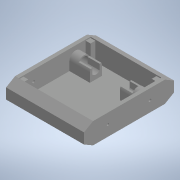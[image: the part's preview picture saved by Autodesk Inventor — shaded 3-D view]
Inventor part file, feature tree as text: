
AUTODESK INVENTOR PART (.ipt)
format: ipt  version: 2020 (Build 240168000, 168)  size: 243,712 bytes
history: native  units: in
note: dims shown in document units (in); Inventor stores cm internally (conversion verified against a paired STEP export)
features: extrude x7, sketch x7, projected_geometry x4, mirror x2
ambient origin geometry x8: Origin, YZ Plane, XZ Plane, XY Plane, X Axis, Y Axis, Z Axis, Center Point
bodies: Solid1 (feature_tree)
feature tree (20):
  extrude  "Extrusion1"  Depth=5.9055in
  extrude  "Extrusion2"  TaperAngle=0.0deg  [1 undecoded]
  extrude  "Extrusion3"  Depth=1.2598in
  extrude  "Extrusion4"  Depth=0.315in
  extrude  "Extrusion5"  TaperAngle=0.0deg  [1 undecoded]
  extrude  "Extrusion6"  Depth=0.689in
  mirror  "Mirror1"
  extrude  "Extrusion7"  Depth=0.0787in
  mirror  "Mirror2"
  sketch  "Sketch1"  dims[d0=1.378in d1=5.9055in]
  sketch  "Sketch2"  dims[d2=5.1181in d3=0.0in]
  projected_geometry  "Projected Loop1"
  sketch  "Sketch3"  dims[d4=0.2362in d5=1.2598in]
  projected_geometry  "Projected Loop2"
  projected_geometry  "Projected Loop3"
  sketch  "Sketch4"  dims[d6=0.0in d8=0.315in]
  sketch  "Sketch5"  dims[d10=1.1898in d11=0.0in]
  projected_geometry  "Projected Loop4"
  sketch  "Sketch6"  dims[d12=0.6496in d13=0.689in]
  sketch  "Sketch7"  dims[d14=1.5748in d15=0.0787in d16=0.5512in d17=0.0in d18=0.6102in d19=0.4803in d20=0.7874in d21=0.0in d22=0.1654in d23=6.063in d24=0.0in d25=0.5967in d26=0.1575in d27=1.5748in d28=0.0in d29=0.0in]
note: 2 required parameter values undecoded (feature->parameter linkage not recoverable at this tier; creation-order binding heuristic only, values carry confidence <= 0.55)
